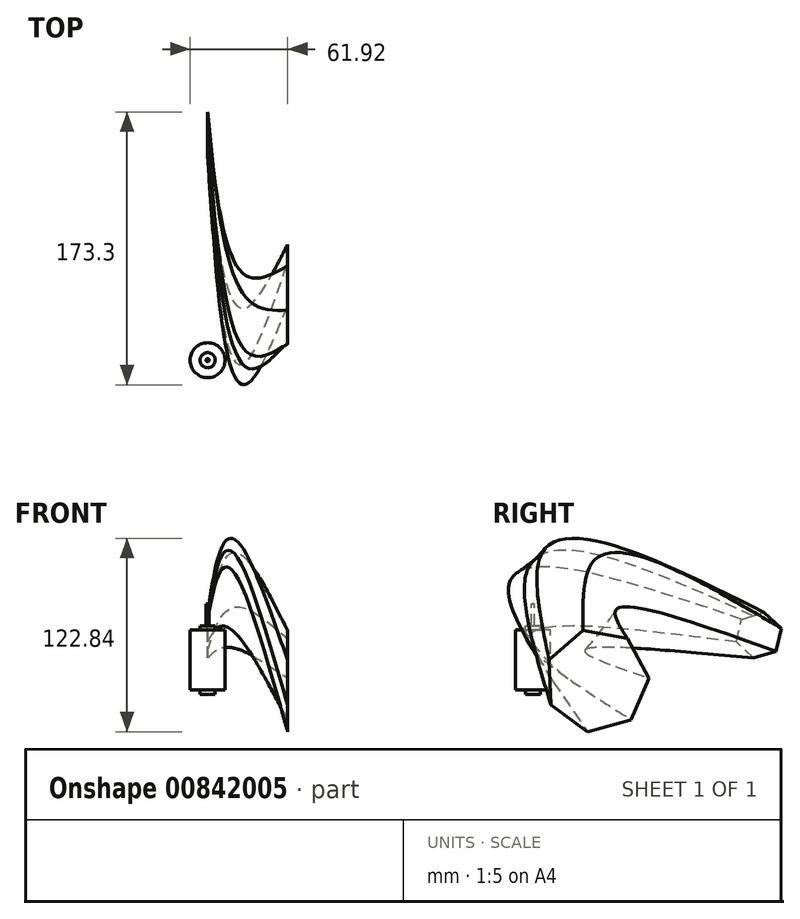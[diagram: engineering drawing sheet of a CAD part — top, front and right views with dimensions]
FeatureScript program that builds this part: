
annotation { "Feature Type Name" : "Feature", "Feature Type Description" : "" }
export const myFeature = defineFeature(function(context is Context, id is Id, definition is map)
    precondition{}
    {
        {
            var Q0;
            Q0=qCreatedBy(makeId("Right.planeOp"),FACE);
            var sketch = newSketch(context, id + "F0", { "sketchPlane" : qUnion([Q0])});
            skLineSegment(sketch, "E0", {"start": v(-59.26, 48.74) * mm, "end": v(-59.26, -8.66) * mm});
            skLineSegment(sketch, "E1", {"start": v(-59.26, -8.66) * mm, "end": v(-54.46, -8.66) * mm});
            skLineSegment(sketch, "E2", {"start": v(-54.46, -8.66) * mm, "end": v(-54.46, -5.96) * mm});
            skLineSegment(sketch, "E3", {"start": v(-54.46, -5.96) * mm, "end": v(-48.14, -5.96) * mm});
            skLineSegment(sketch, "E4", {"start": v(-48.14, -5.96) * mm, "end": v(-48.14, 32.04) * mm});
            skLineSegment(sketch, "E5", {"start": v(-48.14, 32.04) * mm, "end": v(-54.46, 32.04) * mm});
            skLineSegment(sketch, "E6", {"start": v(-54.46, 32.04) * mm, "end": v(-54.46, 34.74) * mm});
            skLineSegment(sketch, "E7", {"start": v(-54.46, 34.74) * mm, "end": v(-58.26, 34.74) * mm});
            skLineSegment(sketch, "E8", {"start": v(-58.26, 34.74) * mm, "end": v(-58.26, 48.74) * mm});
            skLineSegment(sketch, "E9", {"start": v(-58.26, 48.74) * mm, "end": v(-59.26, 48.74) * mm});
            skSolve(sketch);
        }
        {
            var Q0;
            Q0=makeQuery(id+"F0.imprint","IMPRINT",FACE,{"disambiguationData":[TD([[makeQuery(id+"F0.imprint","IMPRINT",EDGE,{"derivedFrom":sQuery(id+"F0.wireOp",EDGE,"E0")}),1.0]])]});
            var Q1;
            Q1=sQuery(id+"F0.wireOp",EDGE,"E0");
            revolve(context, id + "F1", {"surfaceOperationType" : NewSurfaceOperationType.NEW, "entities" : qUnion([Q0]), "axis" : qUnion([Q1]), "revolveType" : RevolveType.FULL});
        }
        {
            var Q0;
            Q0=qCreatedBy(makeId("Right.planeOp"),FACE);
            cPlane(context, id + "F2", {"entities" : qUnion([Q0]), "cplaneType" : CPlaneType.OFFSET, "offset" : 25.8 * mm, "width" : 150 * mm, "height" : 150 * mm});
        }
        {
            var Q0;
            Q0=qCreatedBy(id+"F2.planeOp",FACE);
            cPlane(context, id + "F3", {"entities" : qUnion([Q0]), "cplaneType" : CPlaneType.OFFSET, "offset" : 25 * mm, "width" : 150 * mm, "height" : 150 * mm});
        }
        {
            var Q0;
            Q0=qCreatedBy(makeId("Right.planeOp"),FACE);
            var sketch = newSketch(context, id + "F4", { "sketchPlane" : qUnion([Q0])});
            skCircle(sketch, "E10.cCircle", {"center": v(84.17, 28.78) * mm, "radius": 12.93 * mm, "construction": true});
            skLineSegment(sketch, "E10.0", {"start": v(95.1, 18.61) * mm, "end": v(80.84, 14.23) * mm});
            skLineSegment(sketch, "E10.1", {"start": v(80.84, 14.23) * mm, "end": v(69.9, 24.4) * mm});
            skLineSegment(sketch, "E10.2", {"start": v(69.9, 24.4) * mm, "end": v(73.24, 38.94) * mm});
            skLineSegment(sketch, "E10.3", {"start": v(73.24, 38.94) * mm, "end": v(87.5, 43.33) * mm});
            skLineSegment(sketch, "E10.4", {"start": v(87.5, 43.33) * mm, "end": v(98.44, 33.16) * mm});
            skLineSegment(sketch, "E10.5", {"start": v(98.44, 33.16) * mm, "end": v(95.1, 18.61) * mm});
            skPoint(sketch, "E10.0.midPoint", {"position": v(87.97, 16.42) * mm});
            skSolve(sketch);
        }
        {
            var Q0;
            Q0=qCreatedBy(id+"F3.planeOp",FACE);
            var sketch = newSketch(context, id + "F5", { "sketchPlane" : qUnion([Q0])});
            skCircle(sketch, "E11.cCircle", {"center": v(-18.75, 0) * mm, "radius": 29.73 * mm, "construction": true});
            skLineSegment(sketch, "E11.0", {"start": v(14.21, 1.47) * mm, "end": v(2.95, -24.85) * mm});
            skLineSegment(sketch, "E11.1", {"start": v(2.95, -24.85) * mm, "end": v(-24.65, -32.46) * mm});
            skLineSegment(sketch, "E11.2", {"start": v(-24.65, -32.46) * mm, "end": v(-47.8, -15.63) * mm});
            skLineSegment(sketch, "E11.3", {"start": v(-47.8, -15.63) * mm, "end": v(-49.08, 12.98) * mm});
            skLineSegment(sketch, "E11.4", {"start": v(-49.08, 12.98) * mm, "end": v(-27.52, 31.8) * mm});
            skLineSegment(sketch, "E11.5", {"start": v(-27.52, 31.8) * mm, "end": v(0.65, 26.69) * mm});
            skLineSegment(sketch, "E11.6", {"start": v(0.65, 26.69) * mm, "end": v(14.21, 1.47) * mm});
            skPoint(sketch, "E11.0.midPoint", {"position": v(8.58, -11.7) * mm});
            skSolve(sketch);
        }
        {
            var Q0;
            Q0=qCreatedBy(id+"F2.planeOp",FACE);
            var sketch = newSketch(context, id + "F6", { "sketchPlane" : qUnion([Q0])});
            skCircle(sketch, "E12.cCircle", {"center": v(-40.08, 47.68) * mm, "radius": 29.33 * mm, "construction": true});
            skLineSegment(sketch, "E12.0", {"start": v(-6.3, 45.2) * mm, "end": v(-25.33, 17.19) * mm});
            skLineSegment(sketch, "E12.1", {"start": v(-25.33, 17.19) * mm, "end": v(-59.11, 19.65) * mm});
            skLineSegment(sketch, "E12.2", {"start": v(-59.11, 19.65) * mm, "end": v(-73.87, 50.14) * mm});
            skLineSegment(sketch, "E12.3", {"start": v(-73.87, 50.14) * mm, "end": v(-54.84, 78.17) * mm});
            skLineSegment(sketch, "E12.4", {"start": v(-54.84, 78.17) * mm, "end": v(-21.06, 75.7) * mm});
            skLineSegment(sketch, "E12.5", {"start": v(-21.06, 75.7) * mm, "end": v(-6.3, 45.2) * mm});
            skPoint(sketch, "E12.0.midPoint", {"position": v(-15.82, 31.2) * mm});
            skSolve(sketch);
        }
        {
            var Q0;
            Q0=makeQuery(id+"F4.imprint","IMPRINT",FACE,{"disambiguationData":[TD([[makeQuery(id+"F4.imprint","IMPRINT",EDGE,{"derivedFrom":sQuery(id+"F4.wireOp",EDGE,"E10.0")}),-1.0]])]});
            var Q1;
            Q1=makeQuery(id+"F6.imprint","IMPRINT",FACE,{"disambiguationData":[TD([[makeQuery(id+"F6.imprint","IMPRINT",EDGE,{"derivedFrom":sQuery(id+"F6.wireOp",EDGE,"E12.0")}),-1.0]])]});
            var Q2;
            Q2=makeQuery(id+"F5.imprint","IMPRINT",FACE,{"disambiguationData":[TD([[makeQuery(id+"F5.imprint","IMPRINT",EDGE,{"derivedFrom":sQuery(id+"F5.wireOp",EDGE,"E11.0")}),-1.0]])]});
            loft(context, id + "F7", {"sheetProfilesArray" : [{ "sheetProfileEntities" : qUnion([Q0]) }, { "sheetProfileEntities" : qUnion([Q1]) }, { "sheetProfileEntities" : qUnion([Q2]) }]});
        }
    });
